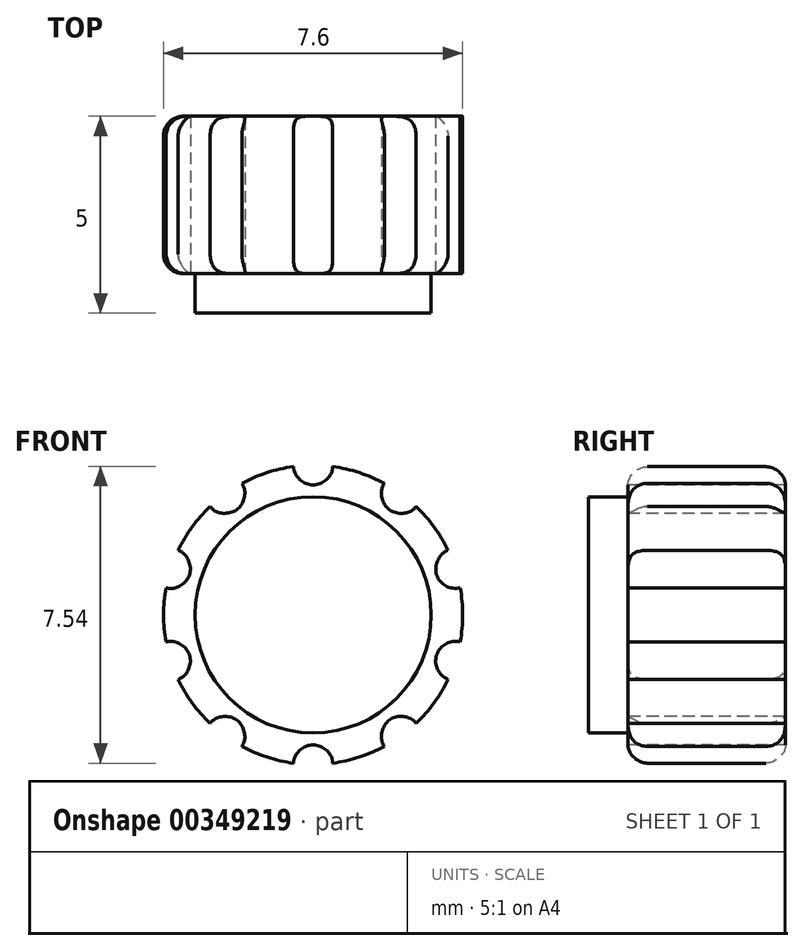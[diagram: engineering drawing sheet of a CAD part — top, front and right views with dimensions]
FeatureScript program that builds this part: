
annotation { "Feature Type Name" : "Feature", "Feature Type Description" : "" }
export const myFeature = defineFeature(function(context is Context, id is Id, definition is map)
    precondition{}
    {
        {
            var Q0;
            Q0=qCreatedBy(makeId("Front.planeOp"),FACE);
            var sketch = newSketch(context, id + "F0", { "sketchPlane" : qUnion([Q0])});
            skCircle(sketch, "E0", {"center": v(0, 0) * mm, "radius": 3.8 * mm});
            skCircle(sketch, "E1", {"center": v(0, 0) * mm, "radius": 3 * mm});
            skLineSegment(sketch, "E2", {"start": v(0, 0) * mm, "end": v(0, 3.8) * mm});
            skCircle(sketch, "E3", {"center": v(0, 3.8) * mm, "radius": 0.5 * mm});
            skCircle(sketch, "E4.1.0", {"center": v(-2.23, 3.07) * mm, "radius": 0.5 * mm});
            skCircle(sketch, "E4.2.0", {"center": v(-3.61, 1.17) * mm, "radius": 0.5 * mm});
            skCircle(sketch, "E4.3.0", {"center": v(-3.61, -1.17) * mm, "radius": 0.5 * mm});
            skCircle(sketch, "E4.4.0", {"center": v(-2.23, -3.07) * mm, "radius": 0.5 * mm});
            skCircle(sketch, "E4.5.0", {"center": v(0, -3.8) * mm, "radius": 0.5 * mm});
            skCircle(sketch, "E4.6.0", {"center": v(2.23, -3.07) * mm, "radius": 0.5 * mm});
            skCircle(sketch, "E4.7.0", {"center": v(3.61, -1.17) * mm, "radius": 0.5 * mm});
            skCircle(sketch, "E5.1.8.0", {"center": v(3.61, 1.17) * mm, "radius": 0.5 * mm});
            skCircle(sketch, "E5.1.9.0", {"center": v(2.23, 3.07) * mm, "radius": 0.5 * mm});
            skSolve(sketch);
        }
        {
            var Q0;
            Q0=makeQuery(id+"F0.imprint","IMPRINT",FACE,{"disambiguationData":[TD([[makeQuery(id+"F0.imprint","IMPRINT",EDGE,{"derivedFrom":sQuery(id+"F0.wireOp",EDGE,"E1")}),1.0]])]});
            var Q1;
            Q1=makeQuery(id+"F0.imprint","IMPRINT",FACE,{"disambiguationData":[TD([[makeQuery(id+"F0.imprint","IMPRINT",EDGE,{"derivedFrom":sQuery(id+"F0.wireOp",EDGE,"E0")}),1.0]])]});
            var Q2;
            Q2=makeQuery(id+"F0.imprint","IMPRINT",FACE,{"disambiguationData":[TD([[makeQuery(id+"F0.imprint","IMPRINT",EDGE,{"derivedFrom":sQuery(id+"F0.wireOp",EDGE,"E1")}),-1.0]])]});
            extrude(context, id + "F1", {"entities" : qUnion([Q0, Q1, Q2]), "oppositeDirection" : true, "depth" : 4 * mm});
        }
        {
            var Q0;
            Q0=makeQuery(id+"F0.imprint","IMPRINT",FACE,{"disambiguationData":[TD([[makeQuery(id+"F0.imprint","IMPRINT",EDGE,{"derivedFrom":sQuery(id+"F0.wireOp",EDGE,"E1")}),1.0]])]});
            extrude(context, id + "F2", {"entities" : qUnion([Q0]), "operationType" : NewBodyOperationType.ADD, "depth" : 1 * mm});
        }
        {
            var Q0;
            {var subQ0=sQuery(id+"F0.wireOp",EDGE,"E0");Q0=makeQuery(id+"F1.opExtrude","CAP_EDGE",EDGE,{"disambiguationData":[OSD([subQ0]),TDD([makeQuery(id+"F0.imprint","IMPRINT",EDGE,{"disambiguationData":[TD([[makeQuery(id+"F0.imprint","INTERSECT",VERTEX,{"disambiguationData":[OD(0.0)],"derivedFrom":[subQ0,sQuery(id+"F0.wireOp",EDGE,"E4.7.0")]}),1.0]])],"derivedFrom":subQ0})])],"isStart":false});}
            var Q1;
            {var subQ0=sQuery(id+"F0.wireOp",EDGE,"E0");Q1=makeQuery(id+"F1.opExtrude","CAP_EDGE",EDGE,{"disambiguationData":[OSD([subQ0]),TDD([makeQuery(id+"F0.imprint","IMPRINT",EDGE,{"disambiguationData":[TD([[makeQuery(id+"F0.imprint","INTERSECT",VERTEX,{"disambiguationData":[OD(1.0)],"derivedFrom":[subQ0,sQuery(id+"F0.wireOp",EDGE,"E4.7.0")]}),-1.0]])],"derivedFrom":subQ0})])],"isStart":false});}
            var Q2;
            {var subQ0=sQuery(id+"F0.wireOp",EDGE,"E0");Q2=makeQuery(id+"F1.opExtrude","CAP_EDGE",EDGE,{"disambiguationData":[OSD([subQ0]),TDD([makeQuery(id+"F0.imprint","IMPRINT",EDGE,{"disambiguationData":[TD([[makeQuery(id+"F0.imprint","INTERSECT",VERTEX,{"disambiguationData":[OD(1.0)],"derivedFrom":[subQ0,sQuery(id+"F0.wireOp",EDGE,"E3")]}),-1.0]])],"derivedFrom":subQ0})])],"isStart":false});}
            var Q3;
            {var subQ0=sQuery(id+"F0.wireOp",EDGE,"E0");Q3=makeQuery(id+"F1.opExtrude","CAP_EDGE",EDGE,{"disambiguationData":[OSD([subQ0]),TDD([makeQuery(id+"F0.imprint","IMPRINT",EDGE,{"disambiguationData":[TD([[makeQuery(id+"F0.imprint","INTERSECT",VERTEX,{"disambiguationData":[OD(1.0)],"derivedFrom":[subQ0,sQuery(id+"F0.wireOp",EDGE,"E4.1.0")]}),-1.0]])],"derivedFrom":subQ0})])],"isStart":false});}
            var Q4;
            {var subQ0=sQuery(id+"F0.wireOp",EDGE,"E0");Q4=makeQuery(id+"F1.opExtrude","CAP_EDGE",EDGE,{"disambiguationData":[OSD([subQ0]),TDD([makeQuery(id+"F0.imprint","IMPRINT",EDGE,{"disambiguationData":[TD([[makeQuery(id+"F0.imprint","INTERSECT",VERTEX,{"disambiguationData":[OD(1.0)],"derivedFrom":[subQ0,sQuery(id+"F0.wireOp",EDGE,"E4.2.0")]}),-1.0]])],"derivedFrom":subQ0})])],"isStart":false});}
            var Q5;
            {var subQ0=sQuery(id+"F0.wireOp",EDGE,"E0");Q5=makeQuery(id+"F1.opExtrude","CAP_EDGE",EDGE,{"disambiguationData":[OSD([subQ0]),TDD([makeQuery(id+"F0.imprint","IMPRINT",EDGE,{"disambiguationData":[TD([[makeQuery(id+"F0.imprint","INTERSECT",VERTEX,{"disambiguationData":[OD(1.0)],"derivedFrom":[subQ0,sQuery(id+"F0.wireOp",EDGE,"E4.3.0")]}),-1.0]])],"derivedFrom":subQ0})])],"isStart":false});}
            var Q6;
            {var subQ0=sQuery(id+"F0.wireOp",EDGE,"E0");Q6=makeQuery(id+"F1.opExtrude","CAP_EDGE",EDGE,{"disambiguationData":[OSD([subQ0]),TDD([makeQuery(id+"F0.imprint","IMPRINT",EDGE,{"disambiguationData":[TD([[makeQuery(id+"F0.imprint","INTERSECT",VERTEX,{"disambiguationData":[OD(1.0)],"derivedFrom":[subQ0,sQuery(id+"F0.wireOp",EDGE,"E4.5.0")]}),-1.0]])],"derivedFrom":subQ0})])],"isStart":false});}
            var Q7;
            {var subQ0=sQuery(id+"F0.wireOp",EDGE,"E0");Q7=makeQuery(id+"F1.opExtrude","CAP_EDGE",EDGE,{"disambiguationData":[OSD([subQ0]),TDD([makeQuery(id+"F0.imprint","IMPRINT",EDGE,{"disambiguationData":[TD([[makeQuery(id+"F0.imprint","INTERSECT",VERTEX,{"disambiguationData":[OD(1.0)],"derivedFrom":[subQ0,sQuery(id+"F0.wireOp",EDGE,"E4.4.0")]}),-1.0]])],"derivedFrom":subQ0})])],"isStart":false});}
            var Q8;
            {var subQ0=sQuery(id+"F0.wireOp",EDGE,"E0");Q8=makeQuery(id+"F1.opExtrude","CAP_EDGE",EDGE,{"disambiguationData":[OSD([subQ0]),TDD([makeQuery(id+"F0.imprint","IMPRINT",EDGE,{"disambiguationData":[TD([[makeQuery(id+"F0.imprint","INTERSECT",VERTEX,{"disambiguationData":[OD(1.0)],"derivedFrom":[subQ0,sQuery(id+"F0.wireOp",EDGE,"E4.2.0")]}),-1.0]])],"derivedFrom":subQ0})])],"isStart":true});}
            var Q9;
            {var subQ0=sQuery(id+"F0.wireOp",EDGE,"E0");Q9=makeQuery(id+"F1.opExtrude","CAP_EDGE",EDGE,{"disambiguationData":[OSD([subQ0]),TDD([makeQuery(id+"F0.imprint","IMPRINT",EDGE,{"disambiguationData":[TD([[makeQuery(id+"F0.imprint","INTERSECT",VERTEX,{"disambiguationData":[OD(1.0)],"derivedFrom":[subQ0,sQuery(id+"F0.wireOp",EDGE,"E4.1.0")]}),-1.0]])],"derivedFrom":subQ0})])],"isStart":true});}
            var Q10;
            {var subQ0=sQuery(id+"F0.wireOp",EDGE,"E0");Q10=makeQuery(id+"F1.opExtrude","CAP_EDGE",EDGE,{"disambiguationData":[OSD([subQ0]),TDD([makeQuery(id+"F0.imprint","IMPRINT",EDGE,{"disambiguationData":[TD([[makeQuery(id+"F0.imprint","INTERSECT",VERTEX,{"disambiguationData":[OD(1.0)],"derivedFrom":[subQ0,sQuery(id+"F0.wireOp",EDGE,"E3")]}),-1.0]])],"derivedFrom":subQ0})])],"isStart":true});}
            var Q11;
            {var subQ0=sQuery(id+"F0.wireOp",EDGE,"E0");Q11=makeQuery(id+"F1.opExtrude","CAP_EDGE",EDGE,{"disambiguationData":[OSD([subQ0]),TDD([makeQuery(id+"F0.imprint","IMPRINT",EDGE,{"disambiguationData":[TD([[makeQuery(id+"F0.imprint","INTERSECT",VERTEX,{"disambiguationData":[OD(1.0)],"derivedFrom":[subQ0,sQuery(id+"F0.wireOp",EDGE,"E4.7.0")]}),-1.0]])],"derivedFrom":subQ0})])],"isStart":true});}
            var Q12;
            {var subQ0=sQuery(id+"F0.wireOp",EDGE,"E0");Q12=makeQuery(id+"F1.opExtrude","CAP_EDGE",EDGE,{"disambiguationData":[OSD([subQ0]),TDD([makeQuery(id+"F0.imprint","IMPRINT",EDGE,{"disambiguationData":[TD([[makeQuery(id+"F0.imprint","INTERSECT",VERTEX,{"disambiguationData":[OD(0.0)],"derivedFrom":[subQ0,sQuery(id+"F0.wireOp",EDGE,"E4.7.0")]}),1.0]])],"derivedFrom":subQ0})])],"isStart":true});}
            var Q13;
            {var subQ0=sQuery(id+"F0.wireOp",EDGE,"E0");Q13=makeQuery(id+"F1.opExtrude","CAP_EDGE",EDGE,{"disambiguationData":[OSD([subQ0]),TDD([makeQuery(id+"F0.imprint","IMPRINT",EDGE,{"disambiguationData":[TD([[makeQuery(id+"F0.imprint","INTERSECT",VERTEX,{"disambiguationData":[OD(1.0)],"derivedFrom":[subQ0,sQuery(id+"F0.wireOp",EDGE,"E4.5.0")]}),-1.0]])],"derivedFrom":subQ0})])],"isStart":true});}
            var Q14;
            {var subQ0=sQuery(id+"F0.wireOp",EDGE,"E0");Q14=makeQuery(id+"F1.opExtrude","CAP_EDGE",EDGE,{"disambiguationData":[OSD([subQ0]),TDD([makeQuery(id+"F0.imprint","IMPRINT",EDGE,{"disambiguationData":[TD([[makeQuery(id+"F0.imprint","INTERSECT",VERTEX,{"disambiguationData":[OD(1.0)],"derivedFrom":[subQ0,sQuery(id+"F0.wireOp",EDGE,"E4.4.0")]}),-1.0]])],"derivedFrom":subQ0})])],"isStart":true});}
            var Q15;
            {var subQ0=sQuery(id+"F0.wireOp",EDGE,"E0");Q15=makeQuery(id+"F1.opExtrude","CAP_EDGE",EDGE,{"disambiguationData":[OSD([subQ0]),TDD([makeQuery(id+"F0.imprint","IMPRINT",EDGE,{"disambiguationData":[TD([[makeQuery(id+"F0.imprint","INTERSECT",VERTEX,{"disambiguationData":[OD(1.0)],"derivedFrom":[subQ0,sQuery(id+"F0.wireOp",EDGE,"E4.3.0")]}),-1.0]])],"derivedFrom":subQ0})])],"isStart":true});}
            var Q16;
            {var subQ0=sQuery(id+"F0.wireOp",EDGE,"E0");Q16=makeQuery(id+"F1.opExtrude","CAP_EDGE",EDGE,{"disambiguationData":[OSD([subQ0]),TDD([makeQuery(id+"F0.imprint","IMPRINT",EDGE,{"disambiguationData":[TD([[makeQuery(id+"F0.imprint","INTERSECT",VERTEX,{"disambiguationData":[OD(1.0)],"derivedFrom":[subQ0,sQuery(id+"F0.wireOp",EDGE,"E5.1.8.0")]}),-1.0]])],"derivedFrom":subQ0})])],"isStart":false});}
            var Q17;
            {var subQ0=sQuery(id+"F0.wireOp",EDGE,"E0");Q17=makeQuery(id+"F1.opExtrude","CAP_EDGE",EDGE,{"disambiguationData":[OSD([subQ0]),TDD([makeQuery(id+"F0.imprint","IMPRINT",EDGE,{"disambiguationData":[TD([[makeQuery(id+"F0.imprint","INTERSECT",VERTEX,{"disambiguationData":[OD(0.0)],"derivedFrom":[subQ0,sQuery(id+"F0.wireOp",EDGE,"E5.1.10.0")]}),1.0]])],"derivedFrom":subQ0})])],"isStart":false});}
            var Q18;
            {var subQ0=sQuery(id+"F0.wireOp",EDGE,"E0");Q18=makeQuery(id+"F1.opExtrude","CAP_EDGE",EDGE,{"disambiguationData":[OSD([subQ0]),TDD([makeQuery(id+"F0.imprint","IMPRINT",EDGE,{"disambiguationData":[TD([[makeQuery(id+"F0.imprint","INTERSECT",VERTEX,{"disambiguationData":[OD(1.0)],"derivedFrom":[subQ0,sQuery(id+"F0.wireOp",EDGE,"E5.1.10.0")]}),-1.0]])],"derivedFrom":subQ0})])],"isStart":false});}
            var Q19;
            {var subQ0=sQuery(id+"F0.wireOp",EDGE,"E0");Q19=makeQuery(id+"F1.opExtrude","CAP_EDGE",EDGE,{"disambiguationData":[OSD([subQ0]),TDD([makeQuery(id+"F0.imprint","IMPRINT",EDGE,{"disambiguationData":[TD([[makeQuery(id+"F0.imprint","INTERSECT",VERTEX,{"disambiguationData":[OD(1.0)],"derivedFrom":[subQ0,sQuery(id+"F0.wireOp",EDGE,"E5.1.11.0")]}),-1.0]])],"derivedFrom":subQ0})])],"isStart":false});}
            var Q20;
            {var subQ0=sQuery(id+"F0.wireOp",EDGE,"E0");Q20=makeQuery(id+"F1.opExtrude","CAP_EDGE",EDGE,{"disambiguationData":[OSD([subQ0]),TDD([makeQuery(id+"F0.imprint","IMPRINT",EDGE,{"disambiguationData":[TD([[makeQuery(id+"F0.imprint","INTERSECT",VERTEX,{"disambiguationData":[OD(1.0)],"derivedFrom":[subQ0,sQuery(id+"F0.wireOp",EDGE,"E5.1.11.0")]}),-1.0]])],"derivedFrom":subQ0})])],"isStart":true});}
            var Q21;
            {var subQ0=sQuery(id+"F0.wireOp",EDGE,"E0");Q21=makeQuery(id+"F1.opExtrude","CAP_EDGE",EDGE,{"disambiguationData":[OSD([subQ0]),TDD([makeQuery(id+"F0.imprint","IMPRINT",EDGE,{"disambiguationData":[TD([[makeQuery(id+"F0.imprint","INTERSECT",VERTEX,{"disambiguationData":[OD(1.0)],"derivedFrom":[subQ0,sQuery(id+"F0.wireOp",EDGE,"E5.1.10.0")]}),-1.0]])],"derivedFrom":subQ0})])],"isStart":true});}
            var Q22;
            {var subQ0=sQuery(id+"F0.wireOp",EDGE,"E0");Q22=makeQuery(id+"F1.opExtrude","CAP_EDGE",EDGE,{"disambiguationData":[OSD([subQ0]),TDD([makeQuery(id+"F0.imprint","IMPRINT",EDGE,{"disambiguationData":[TD([[makeQuery(id+"F0.imprint","INTERSECT",VERTEX,{"disambiguationData":[OD(0.0)],"derivedFrom":[subQ0,sQuery(id+"F0.wireOp",EDGE,"E5.1.10.0")]}),1.0]])],"derivedFrom":subQ0})])],"isStart":true});}
            var Q23;
            {var subQ0=sQuery(id+"F0.wireOp",EDGE,"E0");Q23=makeQuery(id+"F1.opExtrude","CAP_EDGE",EDGE,{"disambiguationData":[OSD([subQ0]),TDD([makeQuery(id+"F0.imprint","IMPRINT",EDGE,{"disambiguationData":[TD([[makeQuery(id+"F0.imprint","INTERSECT",VERTEX,{"disambiguationData":[OD(1.0)],"derivedFrom":[subQ0,sQuery(id+"F0.wireOp",EDGE,"E5.1.8.0")]}),-1.0]])],"derivedFrom":subQ0})])],"isStart":true});}
            var Q24;
            {var subQ0=sQuery(id+"F0.wireOp",EDGE,"E0");Q24=makeQuery(id+"F1.opExtrude","CAP_EDGE",EDGE,{"disambiguationData":[OSD([subQ0]),TDD([makeQuery(id+"F0.imprint","IMPRINT",EDGE,{"disambiguationData":[TD([[makeQuery(id+"F0.imprint","INTERSECT",VERTEX,{"disambiguationData":[OD(0.0)],"derivedFrom":[subQ0,sQuery(id+"F0.wireOp",EDGE,"E5.1.8.0")]}),-1.0]])],"derivedFrom":subQ0})])],"isStart":false});}
            var Q25;
            {var subQ0=sQuery(id+"F0.wireOp",EDGE,"E0");Q25=makeQuery(id+"F1.opExtrude","CAP_EDGE",EDGE,{"disambiguationData":[OSD([subQ0]),TDD([makeQuery(id+"F0.imprint","IMPRINT",EDGE,{"disambiguationData":[TD([[makeQuery(id+"F0.imprint","INTERSECT",VERTEX,{"disambiguationData":[OD(1.0)],"derivedFrom":[subQ0,sQuery(id+"F0.wireOp",EDGE,"E5.1.9.0")]}),-1.0]])],"derivedFrom":subQ0})])],"isStart":false});}
            var Q26;
            {var subQ0=sQuery(id+"F0.wireOp",EDGE,"E0");Q26=makeQuery(id+"F1.opExtrude","CAP_EDGE",EDGE,{"disambiguationData":[OSD([subQ0]),TDD([makeQuery(id+"F0.imprint","IMPRINT",EDGE,{"disambiguationData":[TD([[makeQuery(id+"F0.imprint","INTERSECT",VERTEX,{"disambiguationData":[OD(0.0)],"derivedFrom":[subQ0,sQuery(id+"F0.wireOp",EDGE,"E5.1.8.0")]}),-1.0]])],"derivedFrom":subQ0})])],"isStart":true});}
            var Q27;
            {var subQ0=sQuery(id+"F0.wireOp",EDGE,"E0");Q27=makeQuery(id+"F1.opExtrude","CAP_EDGE",EDGE,{"disambiguationData":[OSD([subQ0]),TDD([makeQuery(id+"F0.imprint","IMPRINT",EDGE,{"disambiguationData":[TD([[makeQuery(id+"F0.imprint","INTERSECT",VERTEX,{"disambiguationData":[OD(1.0)],"derivedFrom":[subQ0,sQuery(id+"F0.wireOp",EDGE,"E5.1.9.0")]}),-1.0]])],"derivedFrom":subQ0})])],"isStart":true});}
            fillet(context, id + "F3", {"entities" : qUnion([Q0, Q1, Q2, Q3, Q4, Q5, Q6, Q7, Q8, Q9, Q10, Q11, Q12, Q13, Q14, Q15, Q16, Q17, Q18, Q19, Q20, Q21, Q22, Q23, Q24, Q25, Q26, Q27]), "radius" : 0.5 * mm, "tangentPropagation" : true, "allowEdgeOverflow" : false});
        }
    });
